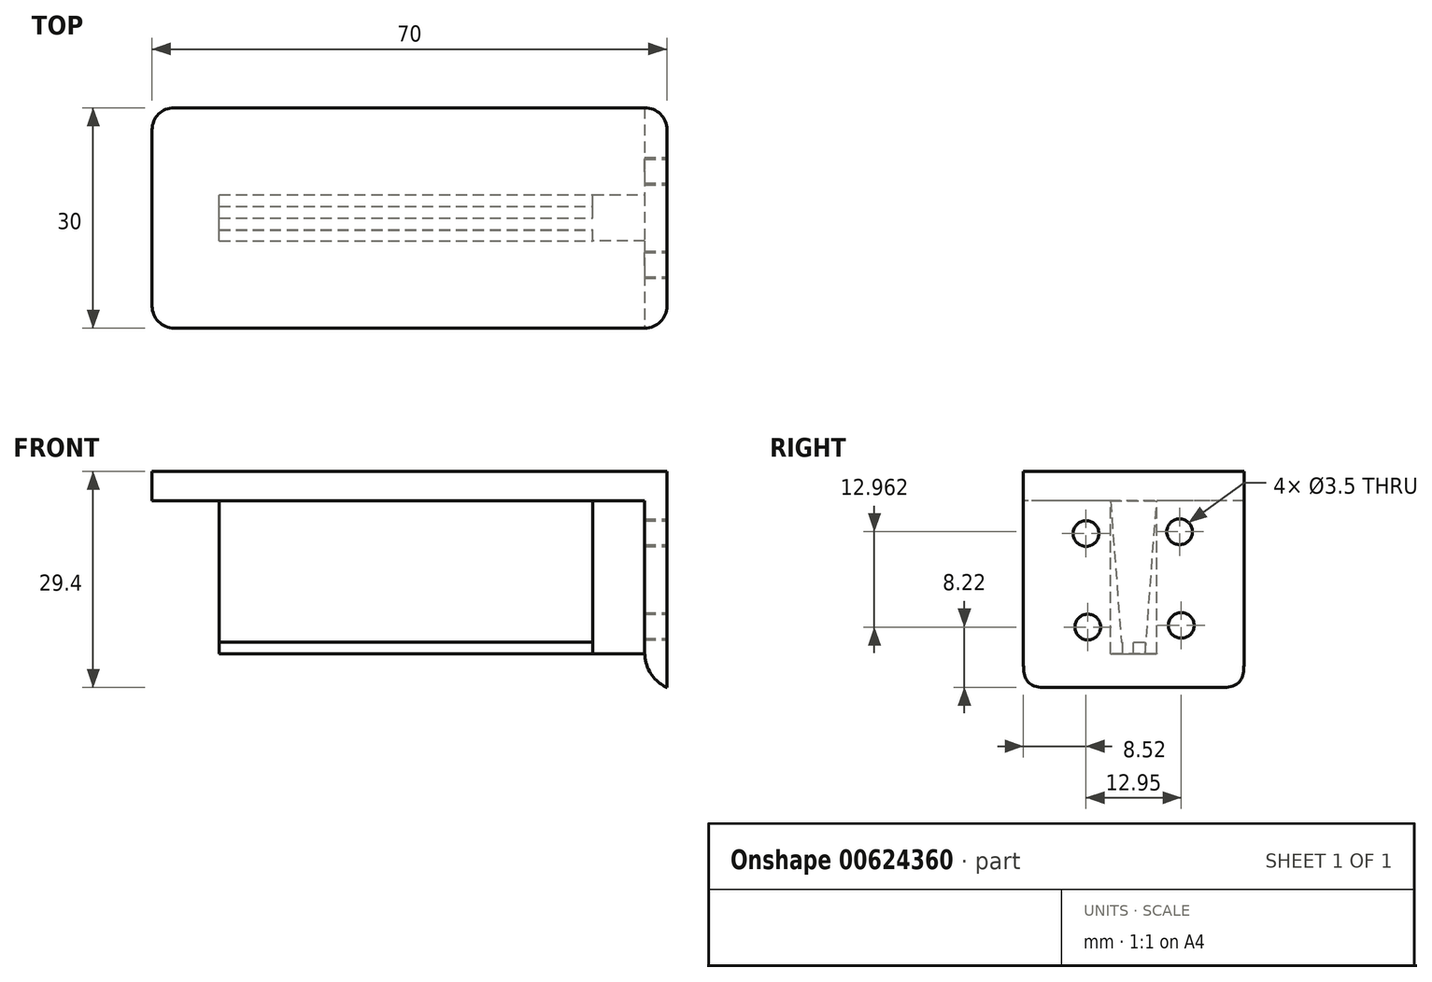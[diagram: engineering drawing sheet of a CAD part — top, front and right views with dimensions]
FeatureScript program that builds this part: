
annotation { "Feature Type Name" : "Feature", "Feature Type Description" : "" }
export const myFeature = defineFeature(function(context is Context, id is Id, definition is map)
    precondition{}
    {
        {
            var Q0;
            Q0=qCreatedBy(makeId("Top.planeOp"),FACE);
            var sketch = newSketch(context, id + "F0", { "sketchPlane" : qUnion([Q0])});
            skLineSegment(sketch, "E0.bottom", {"start": v(-87.28, -14.94) * mm, "end": v(-17.28, -14.94) * mm});
            skLineSegment(sketch, "E0.top", {"start": v(-87.28, -44.94) * mm, "end": v(-17.28, -44.94) * mm});
            skLineSegment(sketch, "E0.left", {"start": v(-87.28, -14.94) * mm, "end": v(-87.28, -44.94) * mm});
            skLineSegment(sketch, "E0.right", {"start": v(-17.28, -14.94) * mm, "end": v(-17.28, -44.94) * mm});
            skSolve(sketch);
        }
        {
            var Q0;
            Q0 = qSketchRegion(id + "F0", true);
            extrude(context, id + "F1", {"entities" : qUnion([Q0]), "depth" : 4 * mm, "offsetDistance" : 25.4 * mm});
        }
        {
            var Q0;
            Q0=makeQuery(id+"F1.opExtrude","SWEPT_EDGE",EDGE,{"disambiguationData":[OSD([sQuery(id+"F0.wireOp",EDGE,"E0.top"),sQuery(id+"F0.wireOp",EDGE,"E0.left")])]});
            fillet(context, id + "F2", {"entities" : qUnion([Q0]), "radius" : 3 * mm, "tangentPropagation" : true, "allowEdgeOverflow" : false});
        }
        {
            var Q0;
            Q0=makeQuery(id+"F1.opExtrude","SWEPT_EDGE",EDGE,{"disambiguationData":[OSD([sQuery(id+"F0.wireOp",EDGE,"E0.bottom"),sQuery(id+"F0.wireOp",EDGE,"E0.left")])]});
            fillet(context, id + "F3", {"entities" : qUnion([Q0]), "radius" : 3 * mm, "tangentPropagation" : true, "allowEdgeOverflow" : false});
        }
        {
            var Q0;
            Q0=makeQuery(id+"F1.opExtrude","SWEPT_EDGE",EDGE,{"disambiguationData":[OSD([sQuery(id+"F0.wireOp",EDGE,"E0.top"),sQuery(id+"F0.wireOp",EDGE,"E0.right")])]});
            fillet(context, id + "F4", {"entities" : qUnion([Q0]), "radius" : 3 * mm, "tangentPropagation" : true, "allowEdgeOverflow" : false});
        }
        {
            var Q0;
            Q0=makeQuery(id+"F1.opExtrude","SWEPT_EDGE",EDGE,{"disambiguationData":[OSD([sQuery(id+"F0.wireOp",EDGE,"E0.bottom"),sQuery(id+"F0.wireOp",EDGE,"E0.right")])]});
            fillet(context, id + "F5", {"entities" : qUnion([Q0]), "radius" : 3 * mm, "tangentPropagation" : true, "allowEdgeOverflow" : false});
        }
        {
            var Q0;
            Q0=makeQuery(id+"F1.opExtrude","CAP_FACE",FACE,{"disambiguationData":[OSD([sQuery(id+"F0.wireOp",EDGE,"E0.bottom"),sQuery(id+"F0.wireOp",EDGE,"E0.top"),sQuery(id+"F0.wireOp",EDGE,"E0.left"),sQuery(id+"F0.wireOp",EDGE,"E0.right")])],"isStart":true});
            var sketch = newSketch(context, id + "F6", { "sketchPlane" : qUnion([Q0])});
            skLineSegment(sketch, "E1", {"start": v(-20.28, 14.94) * mm, "end": v(-20.28, 44.94) * mm});
            skSolve(sketch);
        }
        {
            var Q0;
            Q0=makeQuery(id+"F6.imprint","IMPRINT",FACE,{"disambiguationData":[TD([[makeQuery(id+"F6.imprint","IMPRINT",EDGE,{"derivedFrom":sQuery(id+"F6.wireOp",EDGE,"E1")}),-1.0]])]});
            extrude(context, id + "F7", {"entities" : qUnion([Q0]), "operationType" : NewBodyOperationType.ADD, "depth" : 25.4 * mm, "offsetDistance" : 25.4 * mm});
        }
        {
            var Q0;
            Q0=makeQuery(id+"F7.opExtrude","CAP_EDGE",EDGE,{"disambiguationData":[OSD([sQuery(id+"F6.wireOp",EDGE,"E1")])],"isStart":false});
            fillet(context, id + "F8", {"entities" : qUnion([Q0]), "radius" : 5.08 * mm, "tangentPropagation" : true, "allowEdgeOverflow" : false});
        }
        {
            var Q0;
            {var subQ0=sQuery(id+"F0.wireOp",EDGE,"E0.right");Q0=makeQuery(id+"F7.boolean.opBoolean","MERGE",FACE,{"derivedFrom":[makeQuery(id+"F1.opExtrude","SWEPT_FACE",FACE,{"disambiguationData":[OSD([subQ0])]}),makeQuery(id+"F7.opExtrude","SWEPT_FACE",FACE,{"disambiguationData":[OSD([subQ0])]})]});}
            var sketch = newSketch(context, id + "F9", { "sketchPlane" : qUnion([Q0])});
            skLineSegment(sketch, "E2", {"start": v(-29.94, -10.7) * mm, "end": v(-29.94, -1.2) * mm});
            skLineSegment(sketch, "E3", {"start": v(-29.94, -10.7) * mm, "end": v(-21.44, -10.7) * mm});
            skLineSegment(sketch, "E4", {"start": v(-29.94, -10.7) * mm, "end": v(-38.45, -10.7) * mm});
            skLineSegment(sketch, "E5", {"start": v(-29.94, -10.7) * mm, "end": v(-29.94, -20.2) * mm});
            skCircle(sketch, "E6", {"center": v(-38.45, -10.7) * mm, "radius": 1.36 * mm});
            skCircle(sketch, "E7", {"center": v(-29.94, -1.2) * mm, "radius": 1.5 * mm});
            skCircle(sketch, "E8", {"center": v(-21.44, -10.7) * mm, "radius": 1.5 * mm});
            skCircle(sketch, "E9", {"center": v(-29.94, -20.2) * mm, "radius": 1.5 * mm});
            skLineSegment(sketch, "E10", {"start": v(-29.94, -10.7) * mm, "end": v(-36.42, -4.45) * mm});
            skLineSegment(sketch, "E11", {"start": v(-29.94, -10.7) * mm, "end": v(-23.47, -16.96) * mm});
            skCircle(sketch, "E12", {"center": v(-36.42, -4.45) * mm, "radius": 1.75 * mm});
            skCircle(sketch, "E13", {"center": v(-23.47, -16.96) * mm, "radius": 1.75 * mm});
            skLineSegment(sketch, "E14", {"start": v(-29.94, -10.7) * mm, "end": v(-36.18, -17.18) * mm});
            skLineSegment(sketch, "E15", {"start": v(-29.94, -10.7) * mm, "end": v(-23.7, -4.22) * mm});
            skCircle(sketch, "E16", {"center": v(-36.18, -17.18) * mm, "radius": 1.75 * mm});
            skCircle(sketch, "E17", {"center": v(-23.7, -4.22) * mm, "radius": 1.75 * mm});
            skSolve(sketch);
        }
        {
            var Q0;
            Q0=makeQuery(id+"F9.imprint","IMPRINT",FACE,{"disambiguationData":[TD([[makeQuery(id+"F9.imprint","IMPRINT",EDGE,{"derivedFrom":sQuery(id+"F9.wireOp",EDGE,"E16")}),1.0]])]});
            var Q1;
            Q1=makeQuery(id+"F9.imprint","IMPRINT",FACE,{"disambiguationData":[TD([[makeQuery(id+"F9.imprint","IMPRINT",EDGE,{"derivedFrom":sQuery(id+"F9.wireOp",EDGE,"E12")}),1.0]])]});
            var Q2;
            Q2=makeQuery(id+"F9.imprint","IMPRINT",FACE,{"disambiguationData":[TD([[makeQuery(id+"F9.imprint","IMPRINT",EDGE,{"derivedFrom":sQuery(id+"F9.wireOp",EDGE,"E17")}),1.0]])]});
            var Q3;
            Q3=makeQuery(id+"F9.imprint","IMPRINT",FACE,{"disambiguationData":[TD([[makeQuery(id+"F9.imprint","IMPRINT",EDGE,{"derivedFrom":sQuery(id+"F9.wireOp",EDGE,"E13")}),1.0]])]});
            extrude(context, id + "F10", {"entities" : qUnion([Q0, Q1, Q2, Q3]), "operationType" : NewBodyOperationType.REMOVE, "oppositeDirection" : true, "depth" : 25.4 * mm, "offsetDistance" : 25.4 * mm});
        }
        {
            var Q0;
            Q0=makeQuery(id+"F1.opExtrude","CAP_FACE",FACE,{"disambiguationData":[OSD([sQuery(id+"F0.wireOp",EDGE,"E0.bottom"),sQuery(id+"F0.wireOp",EDGE,"E0.top"),sQuery(id+"F0.wireOp",EDGE,"E0.left"),sQuery(id+"F0.wireOp",EDGE,"E0.right")])],"isStart":true});
            var sketch = newSketch(context, id + "F11", { "sketchPlane" : qUnion([Q0])});
            skLineSegment(sketch, "E18", {"start": v(-20.28, 33.08) * mm, "end": v(-80.43, 33.08) * mm});
            skLineSegment(sketch, "E19", {"start": v(-80.43, 26.8) * mm, "end": v(-20.28, 26.8) * mm});
            skLineSegment(sketch, "E20", {"start": v(-80.43, 33.08) * mm, "end": v(-80.43, 26.8) * mm});
            skLineSegment(sketch, "E21", {"start": v(-20.28, 33.08) * mm, "end": v(-20.28, 26.8) * mm});
            skLineSegment(sketch, "E22", {"start": v(-27.36, 33.08) * mm, "end": v(-27.36, 26.8) * mm});
            skLineSegment(sketch, "E23", {"start": v(-80.43, 33.08) * mm, "end": v(-87.28, 33.08) * mm});
            skLineSegment(sketch, "E24", {"start": v(-80.43, 33.08) * mm, "end": v(-80.43, 44.94) * mm});
            skSolve(sketch);
        }
        {
            var Q0;
            {var subQ0=sQuery(id+"F11.wireOp",EDGE,"E21");Q0=makeQuery(id+"F11.imprint","IMPRINT",FACE,{"disambiguationData":[TD([[makeQuery(id+"F11.imprint","IMPRINT",EDGE,{"derivedFrom":subQ0}),1.0]])]});}
            extrude(context, id + "F12", {"entities" : qUnion([Q0]), "operationType" : NewBodyOperationType.ADD, "depth" : 20.83 * mm, "offsetDistance" : 25.4 * mm});
        }
        {
            var Q0;
            Q0=makeQuery(id+"F12.opExtrude","SWEPT_FACE",FACE,{"disambiguationData":[OSD([sQuery(id+"F11.wireOp",EDGE,"E22")])]});
            var sketch = newSketch(context, id + "F13", { "sketchPlane" : qUnion([Q0])});
            skLineSegment(sketch, "E25", {"start": v(29.94, -20.83) * mm, "end": v(29.94, 0) * mm});
            skLineSegment(sketch, "E26", {"start": v(33.08, -19.21) * mm, "end": v(29.94, -19.21) * mm});
            skLineSegment(sketch, "E27", {"start": v(31.51, -19.21) * mm, "end": v(31.51, -20.83) * mm});
            skLineSegment(sketch, "E28", {"start": v(29.94, -19.21) * mm, "end": v(26.8, -19.21) * mm});
            skLineSegment(sketch, "E29", {"start": v(26.8, -19.21) * mm, "end": v(28.37, -19.21) * mm});
            skLineSegment(sketch, "E30", {"start": v(28.37, -19.21) * mm, "end": v(28.37, -20.83) * mm});
            skLineSegment(sketch, "E31", {"start": v(28.37, -20.83) * mm, "end": v(26.8, 0) * mm});
            skLineSegment(sketch, "E32", {"start": v(26.8, 0) * mm, "end": v(33.08, 0) * mm});
            skLineSegment(sketch, "E33", {"start": v(33.08, 0) * mm, "end": v(31.51, -20.83) * mm});
            skSolve(sketch);
        }
        {
            var Q0;
            {var subQ3=sQuery(id+"F13.wireOp",EDGE,"E28");Q0=makeQuery(id+"F13.imprint","IMPRINT",FACE,{"disambiguationData":[TD([[makeQuery(id+"F13.imprint","IMPRINT",EDGE,{"derivedFrom":subQ3}),1.0]])]});}
            var Q1;
            {var subQ5=sQuery(id+"F13.wireOp",EDGE,"E27");Q1=makeQuery(id+"F13.imprint","IMPRINT",FACE,{"disambiguationData":[TD([[makeQuery(id+"F13.imprint","IMPRINT",EDGE,{"derivedFrom":subQ5}),-1.0]])]});}
            var Q2;
            {var subQ5=sQuery(id+"F13.wireOp",EDGE,"E26");var subQ7=makeQuery(id+"F13.imprint","INTERSECT",VERTEX,{"derivedFrom":[subQ5,sQuery(id+"F13.wireOp",EDGE,"E27")]});Q2=makeQuery(id+"F13.imprint","IMPRINT",FACE,{"disambiguationData":[TD([[makeQuery(id+"F13.imprint","IMPRINT",EDGE,{"disambiguationData":[TD([[subQ7,1.0]])],"derivedFrom":subQ5}),-1.0]])]});}
            var Q3;
            {var subQ1=sQuery(id+"F13.wireOp",EDGE,"E28");Q3=makeQuery(id+"F13.imprint","IMPRINT",FACE,{"disambiguationData":[TD([[makeQuery(id+"F13.imprint","IMPRINT",EDGE,{"derivedFrom":subQ1}),-1.0]])]});}
            extrude(context, id + "F14", {"entities" : qUnion([Q0, Q1, Q2, Q3]), "operationType" : NewBodyOperationType.ADD, "depth" : 50.8 * mm, "offsetDistance" : 25.4 * mm});
        }
    });
